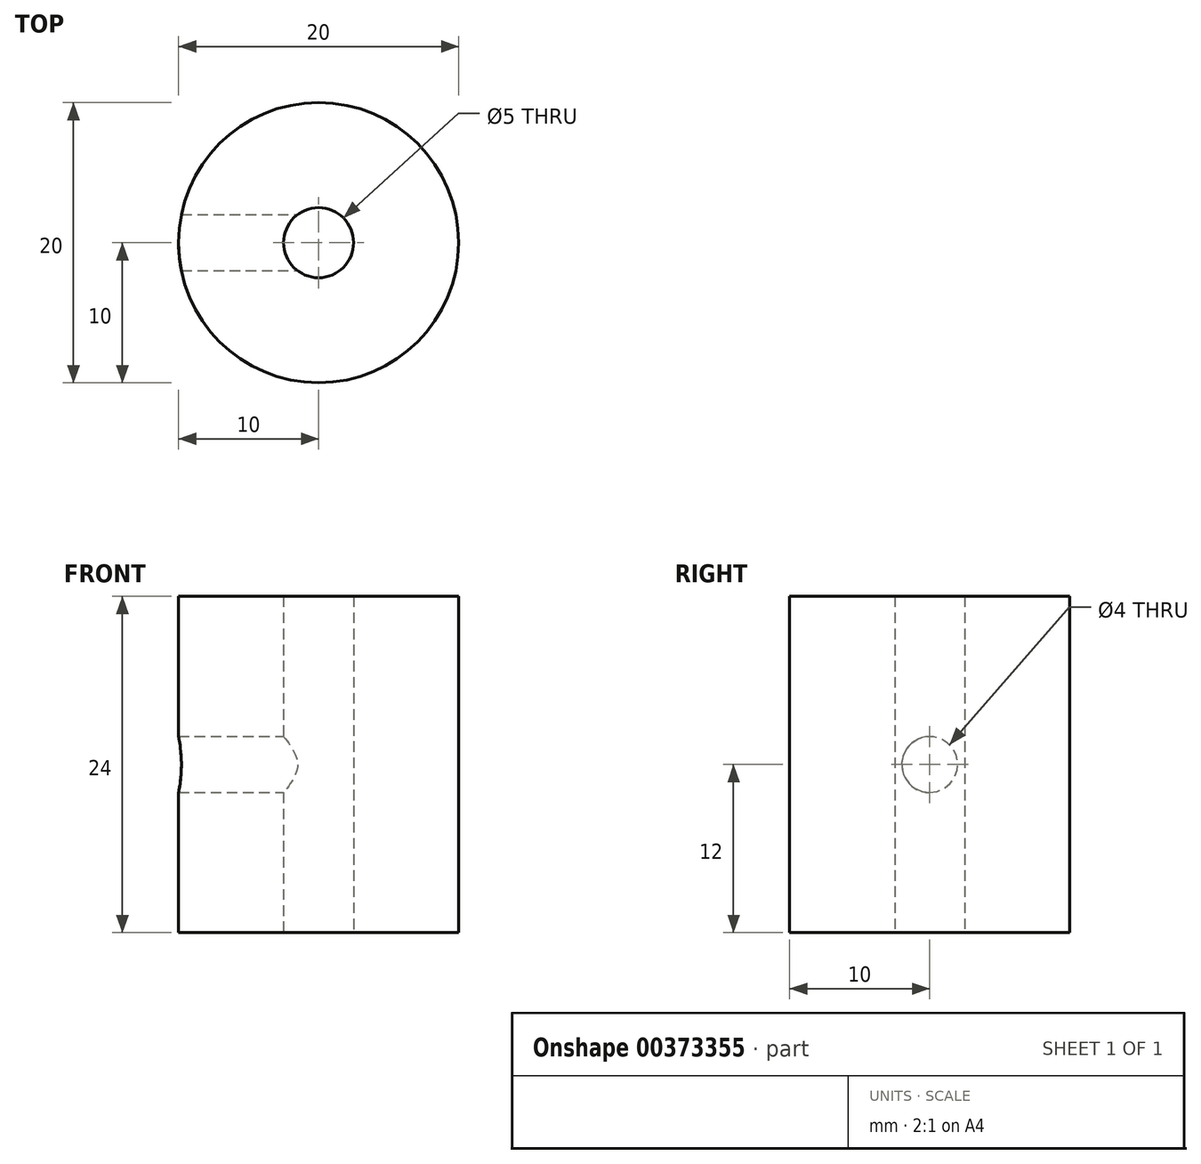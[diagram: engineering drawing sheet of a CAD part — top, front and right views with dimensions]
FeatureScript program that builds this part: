
annotation { "Feature Type Name" : "Feature", "Feature Type Description" : "" }
export const myFeature = defineFeature(function(context is Context, id is Id, definition is map)
    precondition{}
    {
        {
            var Q0;
            Q0=qCreatedBy(makeId("Top.planeOp"),FACE);
            var sketch = newSketch(context, id + "F0", { "sketchPlane" : qUnion([Q0])});
            skCircle(sketch, "E0", {"center": v(0, 0) * mm, "radius": 2.5 * mm});
            skCircle(sketch, "E1", {"center": v(0, 0) * mm, "radius": 10 * mm});
            skSolve(sketch);
        }
        {
            var Q0;
            Q0=makeQuery(id+"F0.imprint","IMPRINT",FACE,{"disambiguationData":[TD([[makeQuery(id+"F0.imprint","IMPRINT",EDGE,{"derivedFrom":sQuery(id+"F0.wireOp",EDGE,"E0")}),-1.0]])]});
            extrude(context, id + "F1", {"entities" : qUnion([Q0]), "depth" : 24 * mm});
        }
        {
            var Q0;
            Q0=qCreatedBy(makeId("Right.planeOp"),FACE);
            var sketch = newSketch(context, id + "F2", { "sketchPlane" : qUnion([Q0])});
            skLineSegment(sketch, "E2", {"start": v(0, 0) * mm, "end": v(0, 12) * mm});
            skCircle(sketch, "E3", {"center": v(0, 12) * mm, "radius": 2 * mm});
            skSolve(sketch);
        }
        {
            var Q0;
            Q0 = qSketchRegion(id + "F2", true);
            extrude(context, id + "F3", {"entities" : qUnion([Q0]), "operationType" : NewBodyOperationType.REMOVE, "oppositeDirection" : true, "depth" : 10 * mm});
        }
    });
